# Revit family: IS_Eurovit_Multiproduct_BIM_NL_K5538;K5539
name_source: partatom
category: Plumbing Fixtures
revit_build: Autodesk Revit MEP 2014 (Build: 20130308_1515(x64)
units: mm (PartAtom-declared; Revit-internal decimal feet)

## types (2) — shared parameters
Accessories = www.idealstandardnederland.nl
AreaUnits = millimeters
Assembly Code = C1030200
AssetType = Vast
BREEAMApproved = No
Brand = Ideal Standard
CodePerformance = DIN EN 13407
ConnectionType = Sanitair
Default Elevation = 870 mm  [stored 2.85433 ft]
DurationUnit = jaar
ECA = No
ExpectedLife = 25
Finish = Wit
IfcExportAs = IfcSanitaryTerminalType
IfcExportType = URINAL
InstallationInstructions = http://www.idealstandardnederland.nl
LinearUnits = millimeters
ManufacturerURL = www.idealstandardnederland.nl
NBSDescription = Wall hung urinals
NBSReference = 45-30-70/350
NettWeight = 12.5 kg
NominalDepth = 336 mm
NominalHeight = 559 mm
NominalLength = 336 mm
NominalWidth = 358 mm
ProductInformation = http://www.idealstandardnederland.nl
Shape = Gesculptuurd
Size = 358 x 336 x 559 mm
Space = Internal
URL = www.idealstandardnederland.nl
Uniclass2015Code = Pr_40_20_93_82
Uniclass2015Title = Wall-hung urinals
Uniclass2015Version = Products v1.1
UrinalColor = White
UrinalMaterial = Vitreous china
UrinalType = Bowl
Version = 1
VolumeUnits = liter
WRAS = No
WarrantyDescription = Fabrieksgarantie
WarrantyDurationParts = 5
WarrantyDurationUnit = jaar
WaterEfficientProduct = No
zero-valued in all types: CWFU, Cost, HWFU, SpilloverLevel, WFU

## per-type parameters (varying)
| type | BIMObjectName | BarCode | Description | Features | K553801 | K553901 | Model | ModelNumber | ModelReference | Name |
| K553801 - EUROVIT URINOIR ACHTERINLAAT  WIT | ISI_IdealStandard_Wall-HungUrinals_K553801 | 4015413929103 | Eurovit urinoir van keramiek. Inclusief bevestigingsset (TT0257919). DIN EN 13407. Toe- en afvoer geïntegreerd of afvoer verticaal naar onder. Voor algemene spoelsystemen. Spoelvolume ca. 0,3 - 0,7 l/sec. Spoelvolume min. 2 l/spoeling. | Urinoir van keramiek. Inclusief bevestigingsset (TT0257919). DIN EN 13407. Toe- en afvoer geïntegreerd of afvoer verticaal naar onder. Voor algemene spoelsystemen. Spoelvolume ca. 0,3 - 0,7 l/sec. Spoelvolume min. 2 l/spoeling. | Yes | No | K553801 | K553801 | Eurovit urinoir van keramiek. Inclusief bevestigingsset (TT0257919). DIN EN 13407. Toe- en afvoer geïntegreerd of afvoer verticaal naar onder. Voor algemene spoelsystemen. Spoelvolume ca. 0,3 - 0,7 l/sec. Spoelvolume min. 2 l/spoeling. | Wall-HungUrinals_K553801_IdealStandard |
| K553901 - EUROVIT URINOIR BOVENINLAAT  WIT | ISI_IdealStandard_Wall-HungUrinals_K553901 | 4015413929110 | Eurovit urinoir van keramiek. Inclusief bevestigingsset (TT0257919). DIN EN 13407. Toevoer vertikaal van boven en afvoer geïntegreerd of afvoer verticaal naar onder. Voor algemene spoelsystemen. Spoelvolume ca. 0,3 - 0,7 l/sec. Spoelvolume min. 2 l/spoeling. | Urinoir van keramiek. Inclusief bevestigingsset (TT0257919). DIN EN 13407. Toevoer vertikaal van boven en afvoer geïntegreerd of afvoer verticaal naar onder. Voor algemene spoelsystemen. Spoelvolume ca. 0,3 - 0,7 l/sec. Spoelvolume min. 2 l/spoeling. | No | Yes | K553901 | K553901 | Eurovit urinoir van keramiek. Inclusief bevestigingsset (TT0257919). DIN EN 13407. Toevoer vertikaal van boven en afvoer geïntegreerd of afvoer verticaal naar onder. Voor algemene spoelsystemen. Spoelvolume ca. 0,3 - 0,7 l/sec. Spoelvolume min. 2 l/spoeling. | Wall-HungUrinals_K553901_IdealStandard |

note: [stored X ft] marks values corroborated as IEEE doubles in the binary element streams (Revit-internal decimal feet)

## geometry (parser evidence)
native form markers: Sweep x1
no freeform markers — native parametric forms only
